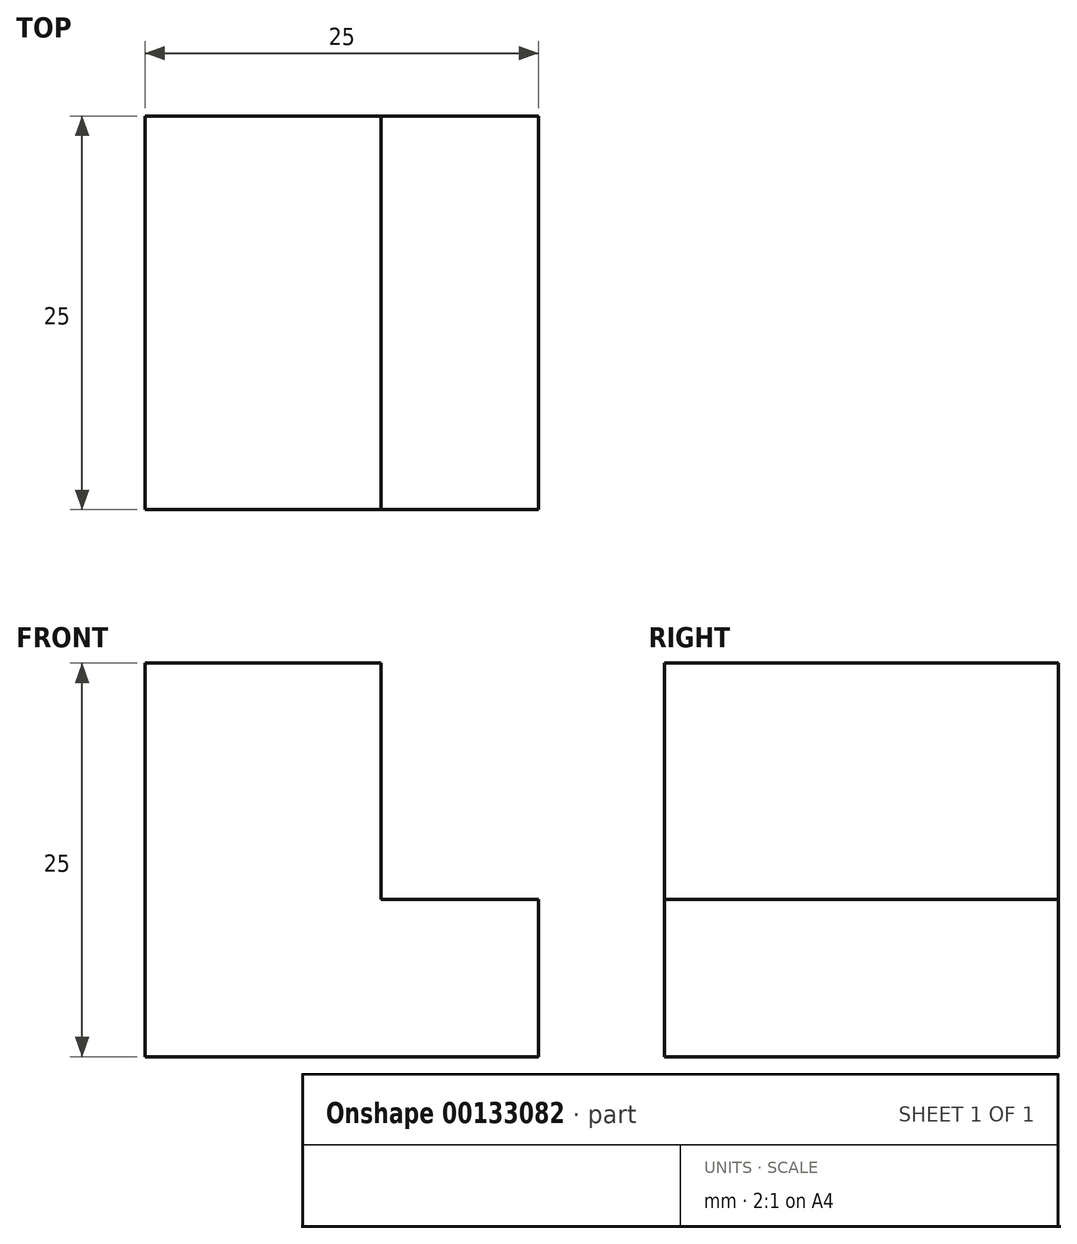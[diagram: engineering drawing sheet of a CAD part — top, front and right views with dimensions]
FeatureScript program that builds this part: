
annotation { "Feature Type Name" : "Feature", "Feature Type Description" : "" }
export const myFeature = defineFeature(function(context is Context, id is Id, definition is map)
    precondition{}
    {
        {
            var Q0;
            Q0=qCreatedBy(makeId("Front.planeOp"),FACE);
            var sketch = newSketch(context, id + "F0", { "sketchPlane" : qUnion([Q0])});
            skLineSegment(sketch, "E0.bottom", {"start": v(24.26, 22.62) * mm, "end": v(-25.74, 22.62) * mm});
            skLineSegment(sketch, "E0.top", {"start": v(24.26, -27.38) * mm, "end": v(-25.74, -27.38) * mm});
            skLineSegment(sketch, "E0.left", {"start": v(24.26, 22.62) * mm, "end": v(24.26, -27.38) * mm});
            skLineSegment(sketch, "E0.right", {"start": v(-25.74, 22.62) * mm, "end": v(-25.74, -27.38) * mm});
            skPoint(sketch, "E0.middle", {"position": v(-0.74, -2.38) * mm});
            skLineSegment(sketch, "E1", {"start": v(-25.74, -2.38) * mm, "end": v(-0.74, -2.38) * mm});
            skLineSegment(sketch, "E2", {"start": v(-25.74, 22.62) * mm, "end": v(-10.74, 22.62) * mm});
            skLineSegment(sketch, "E3", {"start": v(24.26, 22.62) * mm, "end": v(24.26, 7.62) * mm});
            skLineSegment(sketch, "E4", {"start": v(24.26, -27.38) * mm, "end": v(14.26, -27.38) * mm});
            skLineSegment(sketch, "E5", {"start": v(-10.74, 22.62) * mm, "end": v(-10.74, 7.62) * mm});
            skLineSegment(sketch, "E6", {"start": v(-10.74, 7.62) * mm, "end": v(-0.74, 7.62) * mm});
            skLineSegment(sketch, "E7", {"start": v(-0.74, 7.62) * mm, "end": v(-0.74, -2.38) * mm});
            skLineSegment(sketch, "E8", {"start": v(-25.74, -2.38) * mm, "end": v(-25.74, -12.38) * mm});
            skLineSegment(sketch, "E9", {"start": v(-0.74, -2.38) * mm, "end": v(-0.74, -17.38) * mm});
            skLineSegment(sketch, "E10", {"start": v(-0.74, -17.38) * mm, "end": v(-0.74, -2.38) * mm});
            skLineSegment(sketch, "E11", {"start": v(-0.74, -17.38) * mm, "end": v(-10.74, -17.38) * mm});
            skLineSegment(sketch, "E12", {"start": v(-10.74, -17.38) * mm, "end": v(-25.74, -12.38) * mm});
            skLineSegment(sketch, "E13", {"start": v(14.26, -27.38) * mm, "end": v(14.26, -17.38) * mm});
            skLineSegment(sketch, "E14", {"start": v(-0.74, -12.38) * mm, "end": v(6.76, -12.38) * mm});
            skLineSegment(sketch, "E15", {"start": v(6.76, -12.38) * mm, "end": v(6.76, -17.38) * mm});
            skLineSegment(sketch, "E16", {"start": v(6.76, -17.38) * mm, "end": v(14.26, -17.38) * mm});
            skLineSegment(sketch, "E17", {"start": v(-5.74, 7.62) * mm, "end": v(-0.74, 7.62) * mm});
            skLineSegment(sketch, "E18", {"start": v(-5.74, 12.62) * mm, "end": v(24.26, 22.62) * mm});
            skLineSegment(sketch, "E19", {"start": v(24.26, 7.62) * mm, "end": v(24.26, 2.62) * mm});
            skLineSegment(sketch, "E20", {"start": v(24.26, 2.62) * mm, "end": v(4.26, 2.62) * mm});
            skLineSegment(sketch, "E21", {"start": v(4.26, 2.62) * mm, "end": v(-0.74, -2.38) * mm});
            skPoint(sketch, "E22.endSnap0", {"position": v(-5.74, 10.12) * mm});
            skLineSegment(sketch, "E23", {"start": v(-5.74, 12.62) * mm, "end": v(-5.74, 10.12) * mm});
            skLineSegment(sketch, "E24", {"start": v(-5.74, 10.12) * mm, "end": v(-3.24, 10.12) * mm});
            skPoint(sketch, "E24.endSnap0", {"position": v(-3.24, 7.62) * mm});
            skLineSegment(sketch, "E25", {"start": v(-3.24, 10.12) * mm, "end": v(-0.74, 10.12) * mm});
            skLineSegment(sketch, "E26", {"start": v(-0.74, 10.12) * mm, "end": v(-0.74, 7.62) * mm});
            skLineSegment(sketch, "E27", {"start": v(-0.74, 7.62) * mm, "end": v(-0.74, 14.29) * mm});
            skLineSegment(sketch, "E28", {"start": v(4.26, 2.62) * mm, "end": v(-0.74, 2.62) * mm});
            skSolve(sketch);
        }
        {
            var Q0;
            {var subQ2=sQuery(id+"F0.wireOp",EDGE,"E1");Q0=makeQuery(id+"F0.imprint","IMPRINT",FACE,{"disambiguationData":[TD([[makeQuery(id+"F0.imprint","IMPRINT",EDGE,{"derivedFrom":subQ2}),1.0]])]});}
            extrude(context, id + "F1", {"entities" : qUnion([Q0]), "depth" : 25 * mm});
        }
    });
